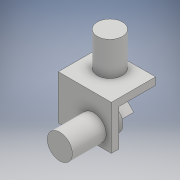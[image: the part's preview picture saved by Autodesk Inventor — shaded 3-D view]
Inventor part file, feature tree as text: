
AUTODESK INVENTOR PART (.ipt)
format: ipt  version: 2018 (Build 220112000, 112)  size: 161,792 bytes
history: native  units: mm
features: extrude x8, sketch x8, projected_geometry x2
ambient origin geometry x8: Origin, YZ Plane, XZ Plane, XY Plane, X Axis, Y Axis, Z Axis, Center Point
bodies: Solid1 (feature_tree)
feature tree (18):
  extrude  "Extrusion1"  Depth=30.0mm
  extrude  "Extrusion2"  Depth=5.0mm
  extrude  "Extrusion3"  Depth=25.0mm
  extrude  "Extrusion4"  TaperAngle=0.0deg  [1 undecoded]
  extrude  "Extrusion5"  Depth=2.0mm
  extrude  "Extrusion6"  Depth=23.0mm
  extrude  "Extrusion7"  TaperAngle=0.0deg  [1 undecoded]
  extrude  "Extrusion8"  TaperAngle=0.0deg  [1 undecoded]
  sketch  "Sketch1"  dims[d0=36.0mm d1=30.0mm]
  sketch  "Sketch2"  dims[d2=5.0mm d3=0.0mm d4=5.0mm]
  sketch  "Sketch3"  dims[d5=25.0mm d6=0.0mm d8=20.5mm]
  sketch  "Sketch4"  dims[d9=3.5mm d11=0.0mm]
  sketch  "Sketch5"  dims[d12=17.0mm d13=2.0mm]
  sketch  "Sketch6"  dims[d14=15.5mm d15=23.0mm]
  sketch  "Sketch7"  dims[d16=0.0mm d18=0.0mm]
  projected_geometry  "Projected Loop1"
  sketch  "Sketch8"  dims[d19=6.38mm d20=0.0mm d24=0.0mm d25=7.0mm d26=1.0mm d27=13.0mm d28=0.0mm]
  projected_geometry  "Projected Loop2"
note: 3 required parameter values undecoded (feature->parameter linkage not recoverable at this tier; creation-order binding heuristic only, values carry confidence <= 0.55)
